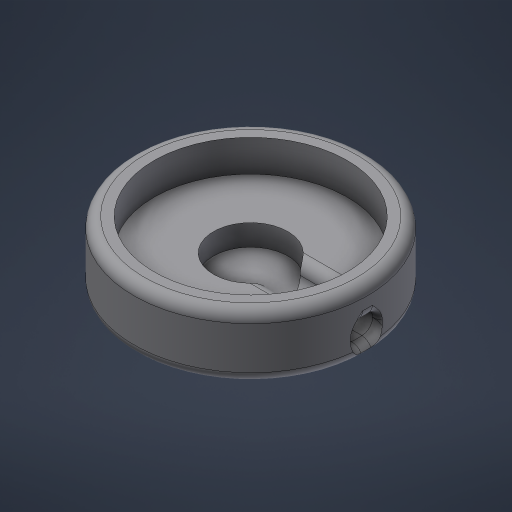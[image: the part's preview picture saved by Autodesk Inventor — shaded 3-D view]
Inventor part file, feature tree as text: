
AUTODESK INVENTOR PART (.ipt)
format: ipt  version: 2023.5 (Build 275446000, 446)  size: 653,824 bytes
history: native  units: mm
features: extrude x3, sketch x1, fillet x1
ambient origin geometry x8: Origin, YZ Plane, XZ Plane, XY Plane, X Axis, Y Axis, Z Axis, Center Point
bodies: Volumenkörper1 (feature_tree)
feature tree (5):
  sketch  "Skizze1"  dims[d0=18.2mm d1=7.0mm d2=3.0mm d3=22.0mm d4=3.0mm d5=0.0mm d6=3.0mm d7=0.0mm d8=2.0mm d9=0.0mm d10=1.0mm]
  extrude  "Extrusion1"  Depth=7.0mm
  extrude  "Extrusion2"  Depth=3.0mm
  extrude  "Extrusion3"  Depth=22.0mm
  fillet  "Rundung1"  Radius=3.0mm
